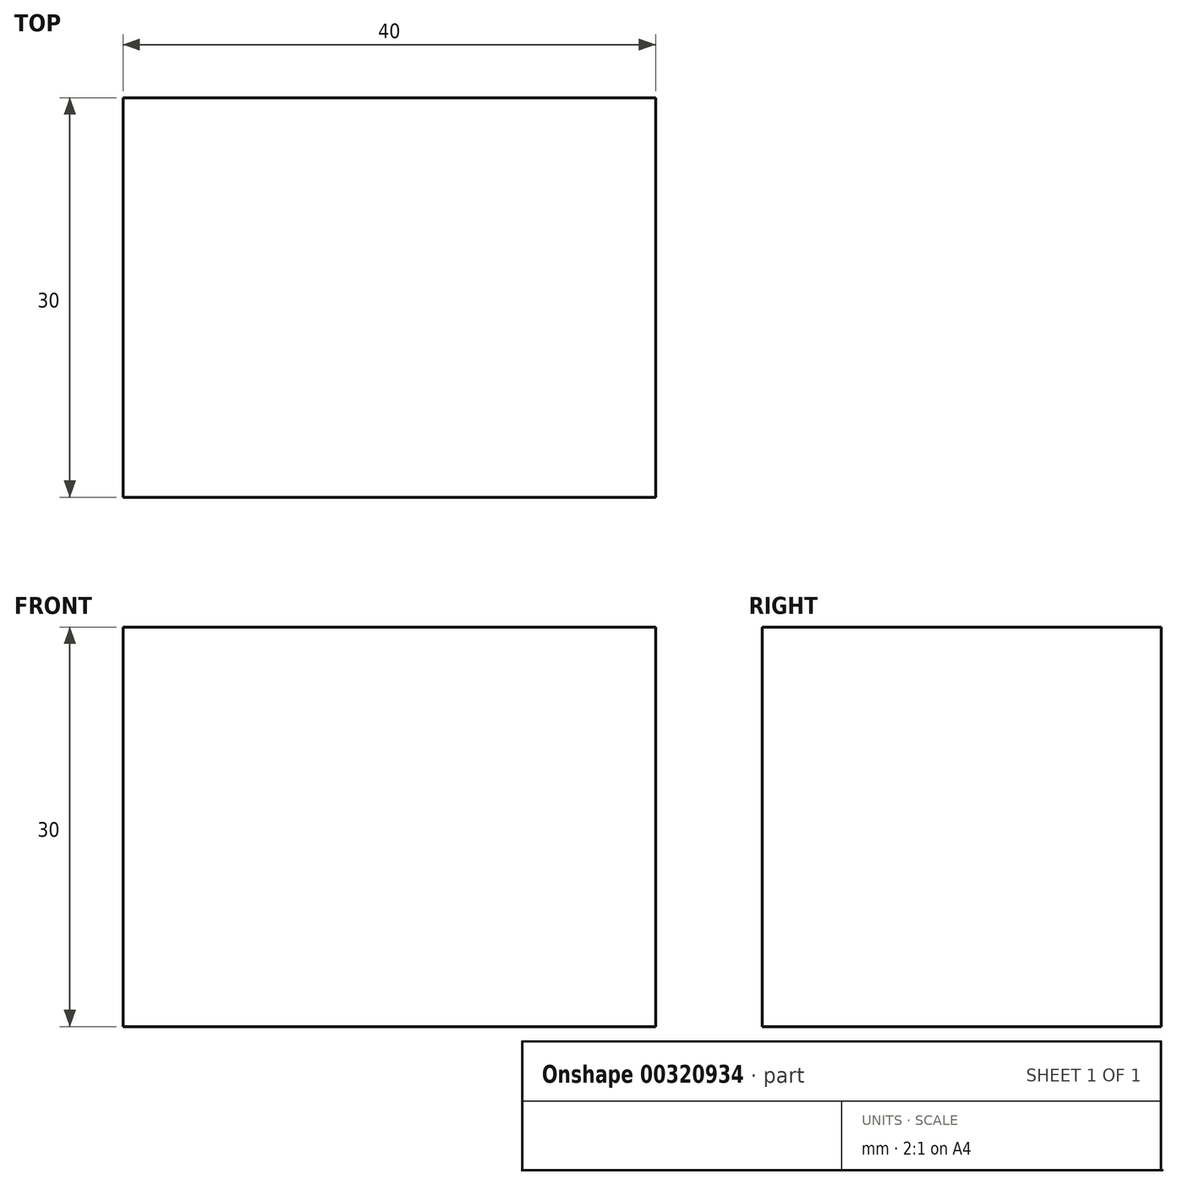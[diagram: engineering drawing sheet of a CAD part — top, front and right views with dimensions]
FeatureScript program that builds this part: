
annotation { "Feature Type Name" : "Feature", "Feature Type Description" : "" }
export const myFeature = defineFeature(function(context is Context, id is Id, definition is map)
    precondition{}
    {
        {
            var Q0;
            Q0=qCreatedBy(makeId("Top.planeOp"),FACE);
            var sketch = newSketch(context, id + "F0", { "sketchPlane" : qUnion([Q0])});
            skLineSegment(sketch, "E0.bottom", {"start": v(-20, 15) * mm, "end": v(20, 15) * mm});
            skLineSegment(sketch, "E0.top", {"start": v(-20, -15) * mm, "end": v(20, -15) * mm});
            skLineSegment(sketch, "E0.left", {"start": v(-20, 15) * mm, "end": v(-20, -15) * mm});
            skLineSegment(sketch, "E0.right", {"start": v(20, 15) * mm, "end": v(20, -15) * mm});
            skPoint(sketch, "E0.middle", {"position": v(0, 0) * mm});
            skSolve(sketch);
        }
        {
            var Q0;
            Q0=makeQuery(id+"F0.imprint","IMPRINT",FACE,{"disambiguationData":[TD([[makeQuery(id+"F0.imprint","IMPRINT",EDGE,{"derivedFrom":sQuery(id+"F0.wireOp",EDGE,"E0.bottom")}),-1.0]])]});
            extrude(context, id + "F1", {"entities" : qUnion([Q0]), "depth" : 30 * mm});
        }
    });
